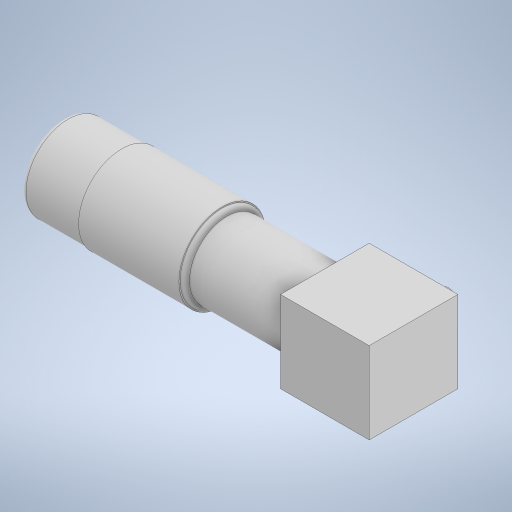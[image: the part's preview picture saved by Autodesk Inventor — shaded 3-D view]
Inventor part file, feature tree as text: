
AUTODESK INVENTOR PART (.ipt)
format: ipt  version: 2024 (Build 280153000, 153)  size: 276,480 bytes
history: native  units: mm
features: extrude x6, plane x1, fillet x1
ambient origin geometry x8: Origin, YZ Plane, XZ Plane, XY Plane, X Axis, Y Axis, Z Axis, Center Point
bodies: Solid1 (feature_tree), Solid2 (feature_tree)
feature tree (8):
  plane  "Work Plane1"
  extrude  "Extrusion1"  Depth=150.0mm
  extrude  "Extrusion2"  Depth=75.0mm
  extrude  "Extrusion3"  Depth=35.0mm
  extrude  "Extrusion4"  Depth=38.0mm
  extrude  "Extrusion5"  Depth=38.0mm TaperAngle=0.0deg
  fillet  "Fillet1"  Radius=32.0mm
  extrude  "Extrusion6"  Depth=42.0mm TaperAngle=0.0deg
